# Revit family: Фильтр-грязевик 4111
name_source: partatom
category: Rohrzubehör
units: mm (PartAtom-declared; Revit-internal decimal feet)

## family parameters
Arbeitsebenenbasiert = Nein
Beim Laden mit Abzugskörper schneiden = Nein
Bemaßung runder Anschluss = Durchmesser verwenden
Gemeinsam genutzt = Nein
Immer vertikal = Ja
OmniClass-Nummer = 23.65.55.14
OmniClass-Titel = Valves for Liquid Services
Teiletyp = Unterbricht

## types (1)
- Фильтр-грязевик 4111
    Hersteller = Herz-Armaturen GmbH
    L03 = 15 mm  [stored 0.0492126 ft]
    L10 = 3.5 mm  [stored 0.0114829 ft]
    L12 = 0.8 mm  [stored 0.00262467 ft]
    R03 = 9.5 mm  [stored 0.031168 ft]
    R100 = 1 mm  [stored 0.00328084 ft]
    SCRNCODE = 05;15;02
    SCRNSEQ = AWI;AWI_TYP="1011";2
    SCTWCODE = 04;16;02
    SCTWSEQ = AW;SBT_TYP_AW="112";2
    URL = www.herz-armaturen.ru
    Vorgabe-Ansicht = 0 mm  [stored 0 ft]
    W01 = 45.00°
    Внутренняя резьба = в соответствии с ISO 228-1
    Заглушка = штампованная латунь CW 617N
    Корпус = литая латунь, устойчивая к селективной цинковой коррозии, CC770S
    Макс. рабочая температура = 110 °C
    Область применения = Фильтры устанавливаются с целью защиты клапанов от мелких частиц грязи в системах отопления и
холодоснабжения. Ароматические хлорированные углеводороды, такие как природный газ или продукты нефтепереработки, разрушают уплотнения из EPDM.
    Среда = Качество теплоносителя в соответствии с ÖNORM H5195 и/или предписаниями VDI-Standard 2035.
Разрешается использование смеси этилен или пропиленгликоля в соотношении 25-50% с водой. Пожалуйста, обратитесь к документации производителя, при использовании этиленгликоля и пропиленгликоля в целях защиты от замерзания. Прокладки EPDM могут быть подвержены воздействию минеральных смазочных масел, что может служить причиной выхода из строя данных уплотнений.
    Уплотнения = EPDM
    Фильтрующий элемент = нержавеющая сталь, размер ячейки 0,75 мм

note: [stored X ft] marks values corroborated as IEEE doubles in the binary element streams (Revit-internal decimal feet)
